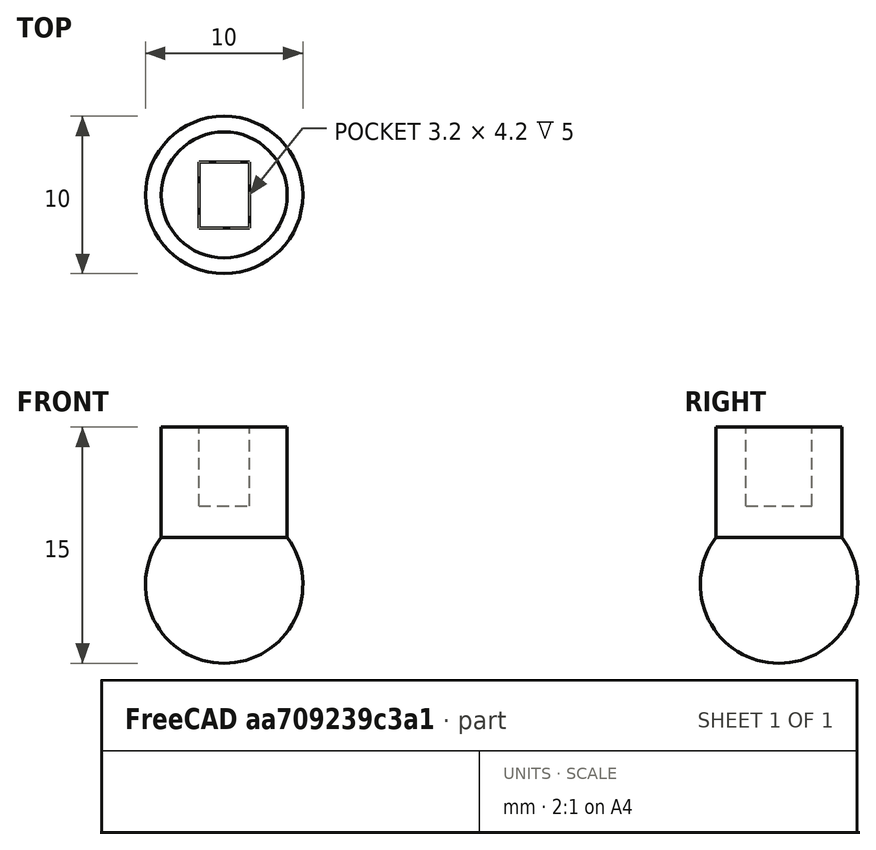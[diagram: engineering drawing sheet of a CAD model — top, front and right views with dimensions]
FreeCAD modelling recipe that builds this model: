
FCSTD DOCUMENT  (FreeCAD 0.20R29410 (Git))
Label: StickEnd
License: All rights reserved
LicenseURL: http://en.wikipedia.org/wiki/All_rights_reserved
objects: Spreadsheet::Sheet×1, Part::Sphere×1, Part::Cylinder×1, Part::Box×1, Part::MultiFuse×1, Part::Cut×1
note: 5 computed .brp shape members not serialized (recipe doc carries the construction recipe); baked Part::Feature solids carry a one-line shape summary decoded from their .brp

FEATURE [Spreadsheet::Sheet] Spreadsheet  label="SS"
  cells = A2=Ball Diameter; B2(BallDiameter)==10mm; A3=Stick Length; B3(StickLength)==5mm; A4=Stick Diameter; B4(StickDiameter)==8mm; A5=Slip X; B5(SlipX)==3.2mm; A6=Slip Y; B6(SlipY)==4.2mm
FEATURE [Part::Sphere] Sphere  label="StickEnd"
  Angle1 = -90
  Angle2 = 90
  Angle3 = 360
  AttacherType = Attacher::AttachEngine3D
  Radius = 5
  expr: Radius = <<SS>>.BallDiameter / 2
FEATURE [Part::Cylinder] Cylinder  label="StickLength"
  Angle = 360
  AttacherType = Attacher::AttachEngine3D
  FirstAngle = 0
  Height = 10
  Radius = 4
  SecondAngle = 0
  expr: .Placement.Base.z = 0mm
  expr: Height = <<SS>>.BallDiameter / 2 + <<SS>>.StickLength
  expr: Radius = <<SS>>.StickDiameter / 2
FEATURE [Part::Box] Box  label="StickRemove"
  AttacherType = Attacher::AttachEngine3D
  Height = 5
  Length = 3.2
  Placement = pos=(-1.6,-2.1,5) rot=(0,0,1;0rad)
  Width = 4.2
  expr: .Placement.Base.x = -<<SS>>.SlipX / 2
  expr: .Placement.Base.y = -<<SS>>.SlipY / 2
  expr: .Placement.Base.z = <<SS>>.BallDiameter / 2
  expr: Height = <<SS>>.StickLength
  expr: Length = <<SS>>.SlipX
  expr: Width = <<SS>>.SlipY
FEATURE [Part::MultiFuse] Fusion  label="StickBody"
  Shapes = -> [Sphere,Cylinder]
FEATURE [Part::Cut] Cut  label="StickTotal"
  Base = -> Fusion
  Tool = -> Box
